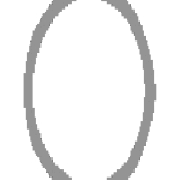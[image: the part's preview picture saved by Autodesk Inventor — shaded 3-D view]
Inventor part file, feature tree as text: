
AUTODESK INVENTOR PART (.ipt)
format: ipt  version: 2021 (Build 250183000, 183)  size: 112,640 bytes
history: native  units: in
note: dims shown in document units (in); Inventor stores cm internally (conversion verified against a paired STEP export)
features: other x4, sketch x3, plane x1
ambient origin geometry x8: Origin, YZ Plane, XZ Plane, XY Plane, X Axis, Y Axis, Z Axis, Center Point
bodies: Solid1 (feature_tree), Body (feature_tree)
feature tree (8):
  other  "Driven Length"
  other  "Frame Generator"
  other  "Start Plane"
  other  "End Plane"
  sketch  "Sketch"  dims[d2=12.431in d4=-0.0in d5=12.431in d6=0.12in d7=0.0in d8=90.0deg d9=12.431in]
  sketch  "Sketch2"  dims[d0=1.0in]
  plane  "Work Plane3"
  sketch  "Sketch3"  dims[d1=0.065in]
